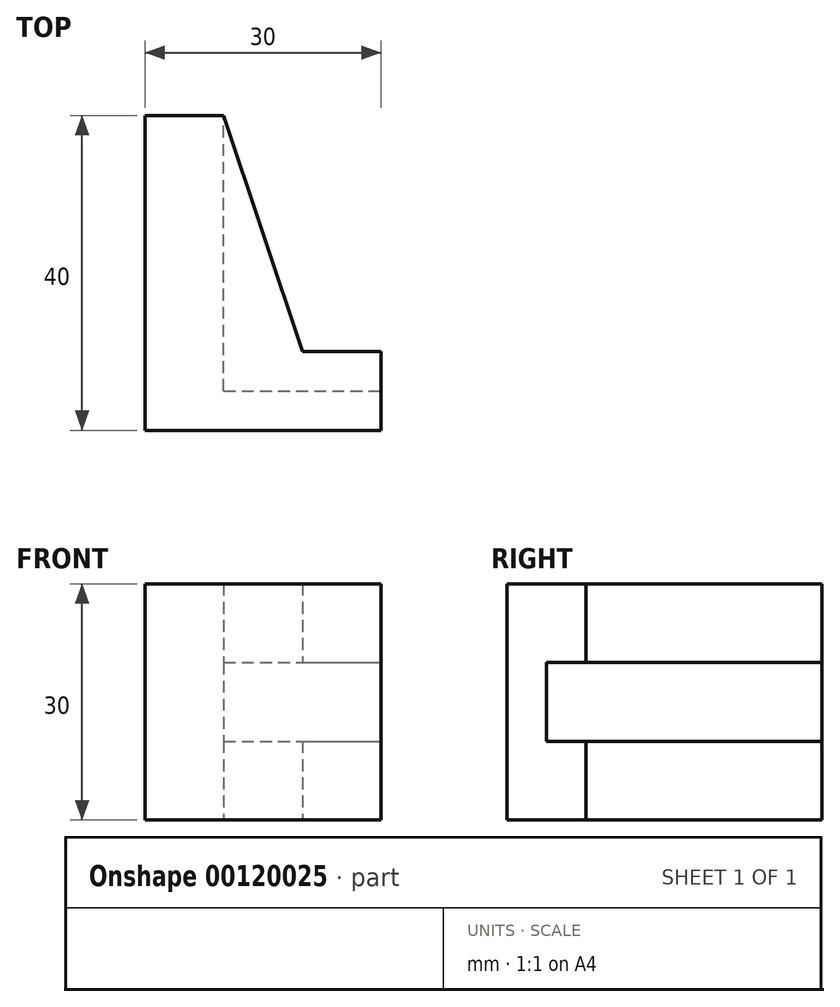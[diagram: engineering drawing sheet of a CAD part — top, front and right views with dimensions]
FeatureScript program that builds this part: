
annotation { "Feature Type Name" : "Feature", "Feature Type Description" : "" }
export const myFeature = defineFeature(function(context is Context, id is Id, definition is map)
    precondition{}
    {
        {
            var Q0;
            Q0=qCreatedBy(makeId("Top.planeOp"),FACE);
            var sketch = newSketch(context, id + "F0", { "sketchPlane" : qUnion([Q0])});
            skLineSegment(sketch, "E0", {"start": v(-27.59, 44.58) * mm, "end": v(-17.59, 44.58) * mm});
            skLineSegment(sketch, "E1", {"start": v(-17.59, 44.58) * mm, "end": v(-7.59, 14.58) * mm});
            skLineSegment(sketch, "E2", {"start": v(-7.59, 14.58) * mm, "end": v(2.41, 14.58) * mm});
            skLineSegment(sketch, "E3", {"start": v(2.41, 14.58) * mm, "end": v(2.41, 4.58) * mm});
            skLineSegment(sketch, "E4", {"start": v(2.41, 4.58) * mm, "end": v(-27.59, 4.58) * mm});
            skLineSegment(sketch, "E5", {"start": v(-27.59, 4.58) * mm, "end": v(-27.59, 44.58) * mm});
            skSolve(sketch);
        }
        {
            var Q0;
            Q0 = qSketchRegion(id + "F0", true);
            extrude(context, id + "F1", {"entities" : qUnion([Q0]), "depth" : 30 * mm});
        }
        {
            var Q0;
            Q0=makeQuery(id+"F1.opExtrude","SWEPT_FACE",FACE,{"disambiguationData":[OSD([sQuery(id+"F0.wireOp",EDGE,"E0")])]});
            var sketch = newSketch(context, id + "F2", { "sketchPlane" : qUnion([Q0])});
            skLineSegment(sketch, "E6.bottom", {"start": v(17.59, 20) * mm, "end": v(-12.41, 20) * mm});
            skLineSegment(sketch, "E6.top", {"start": v(17.59, 10) * mm, "end": v(-12.41, 10) * mm});
            skLineSegment(sketch, "E6.left", {"start": v(17.59, 20) * mm, "end": v(17.59, 10) * mm});
            skLineSegment(sketch, "E6.right", {"start": v(-12.41, 20) * mm, "end": v(-12.41, 10) * mm});
            skSolve(sketch);
        }
        {
            var Q0;
            Q0 = qSketchRegion(id + "F2", true);
            extrude(context, id + "F3", {"entities" : qUnion([Q0]), "operationType" : NewBodyOperationType.REMOVE, "oppositeDirection" : true, "depth" : 35 * mm});
        }
    });
